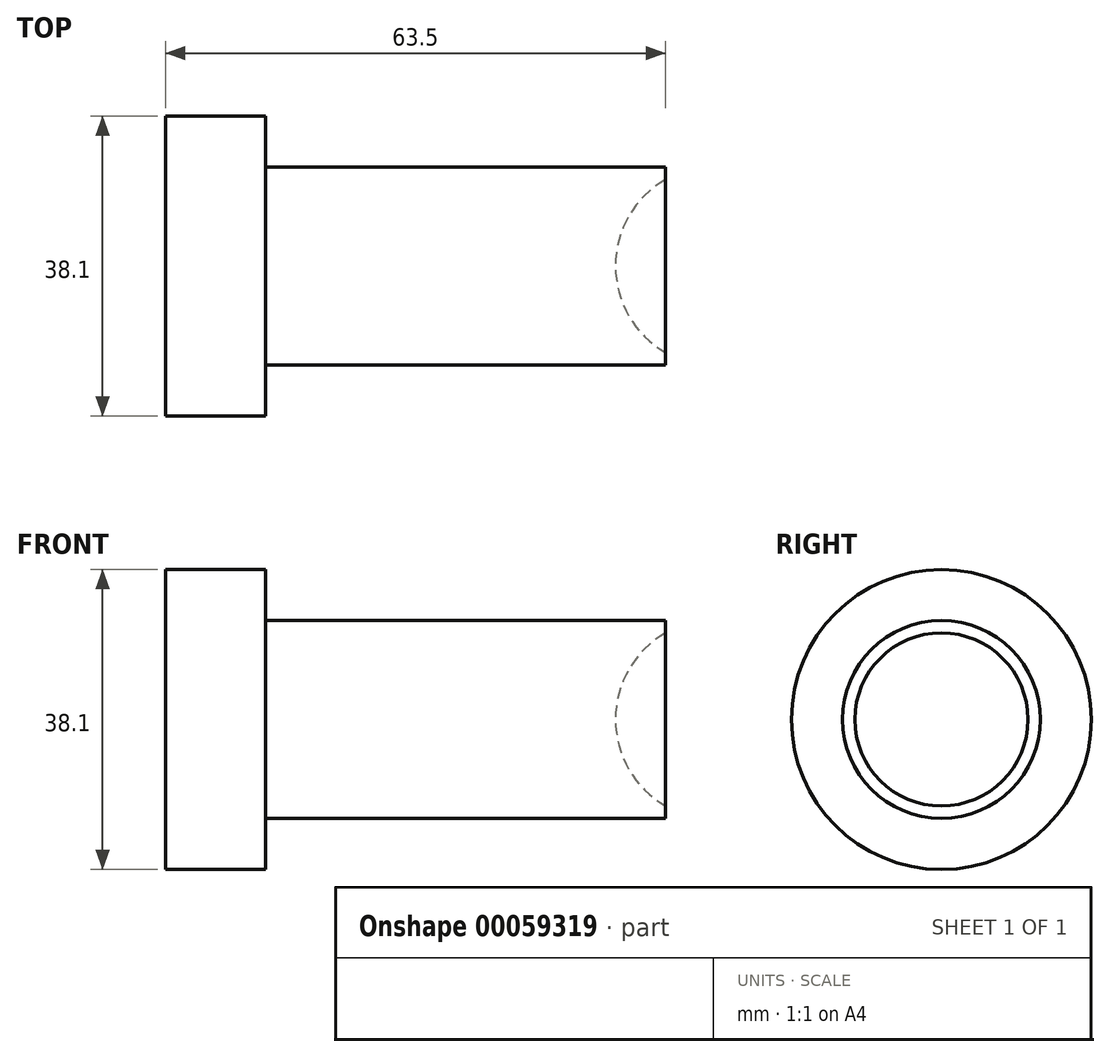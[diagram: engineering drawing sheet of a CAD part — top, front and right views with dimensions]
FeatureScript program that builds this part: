
annotation { "Feature Type Name" : "Feature", "Feature Type Description" : "" }
export const myFeature = defineFeature(function(context is Context, id is Id, definition is map)
    precondition{}
    {
        {
            var Q0;
            Q0=qCreatedBy(makeId("Right.planeOp"),FACE);
            var sketch = newSketch(context, id + "F0", { "sketchPlane" : qUnion([Q0])});
            skCircle(sketch, "E0", {"center": v(0, 0) * mm, "radius": 19.05 * mm});
            skSolve(sketch);
        }
        {
            var Q0;
            Q0=makeQuery(id+"F0.imprint","IMPRINT",FACE,{"disambiguationData":[TD([[makeQuery(id+"F0.imprint","IMPRINT",EDGE,{"derivedFrom":sQuery(id+"F0.wireOp",EDGE,"E0")}),1.0]])]});
            extrude(context, id + "F1", {"entities" : qUnion([Q0]), "depth" : 12.7 * mm});
        }
        {
            var Q0;
            Q0=makeQuery(id+"F1.opExtrude","CAP_FACE",FACE,{"disambiguationData":[OSD([sQuery(id+"F0.wireOp",EDGE,"E0")])],"isStart":false});
            var sketch = newSketch(context, id + "F2", { "sketchPlane" : qUnion([Q0])});
            skCircle(sketch, "E1", {"center": v(0, 0) * mm, "radius": 12.57 * mm});
            skSolve(sketch);
        }
        {
            var Q0;
            Q0=makeQuery(id+"F2.imprint","IMPRINT",FACE,{"disambiguationData":[TD([[makeQuery(id+"F2.imprint","IMPRINT",EDGE,{"derivedFrom":sQuery(id+"F2.wireOp",EDGE,"E1")}),1.0]])]});
            extrude(context, id + "F3", {"entities" : qUnion([Q0]), "operationType" : NewBodyOperationType.ADD, "depth" : 50.8 * mm});
        }
        {
            var Q0;
            Q0=makeQuery(id+"F3.opExtrude","CAP_FACE",FACE,{"disambiguationData":[OSD([sQuery(id+"F2.wireOp",EDGE,"E1")])],"isStart":false});
            cPlane(context, id + "F4", {"entities" : qUnion([Q0]), "cplaneType" : CPlaneType.OFFSET, "offset" : 6.35 * mm, "width" : 152.4 * mm, "height" : 152.4 * mm});
        }
        {
            var Q0;
            Q0=qCreatedBy(id+"F4.planeOp",FACE);
            var sketch = newSketch(context, id + "F5", { "sketchPlane" : qUnion([Q0])});
            skArc(sketch, "E2", {"start": v(0, -12.7) * mm, "mid": v(12.7, 0) * mm, "end": v(0, 12.7) * mm});
            skLineSegment(sketch, "E3", {"start": v(0, 12.7) * mm, "end": v(0, -12.7) * mm});
            skSolve(sketch);
        }
        {
            var Q0;
            Q0=makeQuery(id+"F5.imprint","IMPRINT",FACE,{"disambiguationData":[TD([[makeQuery(id+"F5.imprint","IMPRINT",EDGE,{"derivedFrom":sQuery(id+"F5.wireOp",EDGE,"E2")}),1.0]])]});
            var Q1;
            Q1=sQuery(id+"F5.wireOp",EDGE,"E3");
            revolve(context, id + "F6", {"operationType" : NewBodyOperationType.REMOVE, "entities" : qUnion([Q0]), "axis" : qUnion([Q1]), "revolveType" : RevolveType.FULL, "oppositeDirection" : true});
        }
    });
